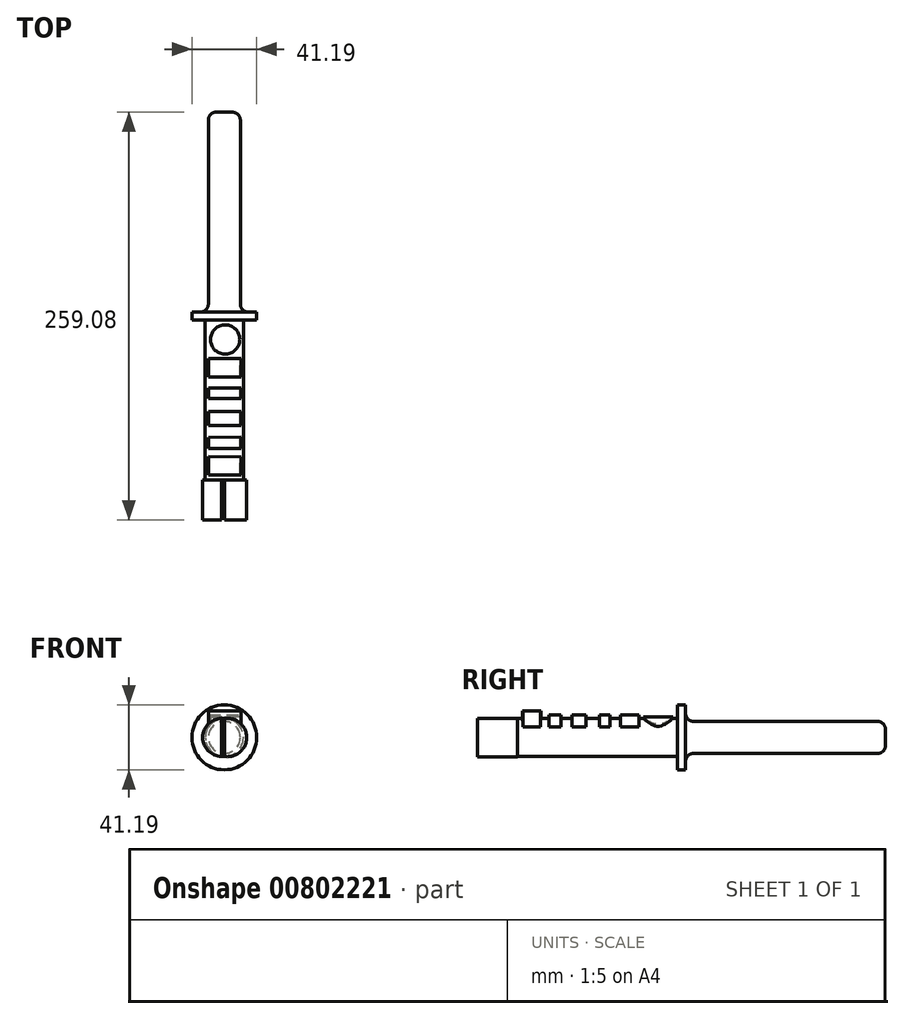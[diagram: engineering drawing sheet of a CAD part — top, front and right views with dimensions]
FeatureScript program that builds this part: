
annotation { "Feature Type Name" : "Feature", "Feature Type Description" : "" }
export const myFeature = defineFeature(function(context is Context, id is Id, definition is map)
    precondition{}
    {
        {
            var Q0;
            Q0=qCreatedBy(makeId("Front.planeOp"),FACE);
            var sketch = newSketch(context, id + "F0", { "sketchPlane" : qUnion([Q0])});
            skCircle(sketch, "E0", {"center": v(-7.9, -6.74) * mm, "radius": 12.12 * mm});
            skSolve(sketch);
        }
        {
            var Q0;
            Q0 = qSketchRegion(id + "F0", true);
            extrude(context, id + "F1", {"entities" : qUnion([Q0]), "depth" : 101.6 * mm, "offsetDistance" : 25.4 * mm});
        }
        {
            var Q0;
            Q0=makeQuery(id+"F1.opExtrude","CAP_FACE",FACE,{"disambiguationData":[OSD([sQuery(id+"F0.wireOp",EDGE,"E0")])],"isStart":true});
            var sketch = newSketch(context, id + "F2", { "sketchPlane" : qUnion([Q0])});
            skCircle(sketch, "E1", {"center": v(7.9, -6.74) * mm, "radius": 20.6 * mm});
            skSolve(sketch);
        }
        {
            var Q0;
            Q0 = qSketchRegion(id + "F2", true);
            extrude(context, id + "F3", {"entities" : qUnion([Q0]), "operationType" : NewBodyOperationType.ADD, "depth" : 5.08 * mm, "offsetDistance" : 25.4 * mm});
        }
        {
            var Q0;
            Q0=makeQuery(id+"F3.opExtrude","CAP_FACE",FACE,{"disambiguationData":[OSD([sQuery(id+"F2.wireOp",EDGE,"E1")])],"isStart":false});
            var sketch = newSketch(context, id + "F4", { "sketchPlane" : qUnion([Q0])});
            skCircle(sketch, "E2", {"center": v(7.9, -6.74) * mm, "radius": 10.16 * mm});
            skSolve(sketch);
        }
        {
            var Q0;
            Q0 = qSketchRegion(id + "F4", true);
            extrude(context, id + "F5", {"entities" : qUnion([Q0]), "operationType" : NewBodyOperationType.ADD, "depth" : 127 * mm, "offsetDistance" : 25.4 * mm});
        }
        {
            var Q0;
            Q0=makeQuery(id+"F5.opExtrude","CAP_EDGE",EDGE,{"disambiguationData":[OSD([sQuery(id+"F4.wireOp",EDGE,"E2")])],"isStart":false});
            var Q1;
            Q1=makeQuery(id+"F5.opExtrude","SWEPT_FACE",FACE,{"disambiguationData":[OSD([sQuery(id+"F4.wireOp",EDGE,"E2")])]});
            fillet(context, id + "F6", {"entities" : qUnion([Q0, Q1]), "radius" : 5.08 * mm, "tangentPropagation" : true, "allowEdgeOverflow" : false});
        }
        {
            var Q0;
            Q0=makeQuery(id+"F1.opExtrude","CAP_FACE",FACE,{"disambiguationData":[OSD([sQuery(id+"F0.wireOp",EDGE,"E0")])],"isStart":false});
            var sketch = newSketch(context, id + "F7", { "sketchPlane" : qUnion([Q0])});
            skLineSegment(sketch, "E3", {"start": v(-7.7, -18.85) * mm, "end": v(-7.7, 5.26) * mm});
            skArc(sketch, "E4", {"start": v(-7.7, -18.85) * mm, "mid": v(6.3, -6.8) * mm, "end": v(-7.7, 5.26) * mm});
            skSolve(sketch);
        }
        {
            var Q0;
            Q0 = qSketchRegion(id + "F7", true);
            extrude(context, id + "F8", {"entities" : qUnion([Q0]), "operationType" : NewBodyOperationType.ADD, "depth" : 25.4 * mm, "offsetDistance" : 25.4 * mm});
        }
        {
            var Q0;
            Q0=makeQuery(id+"F1.opExtrude","CAP_FACE",FACE,{"disambiguationData":[OSD([sQuery(id+"F0.wireOp",EDGE,"E0")])],"isStart":false});
            var sketch = newSketch(context, id + "F9", { "sketchPlane" : qUnion([Q0])});
            skLineSegment(sketch, "E5", {"start": v(-9.73, 5.24) * mm, "end": v(-9.73, -18.71) * mm});
            skArc(sketch, "E6", {"start": v(-9.73, 5.24) * mm, "mid": v(-21.63, -6.74) * mm, "end": v(-9.73, -18.71) * mm});
            skSolve(sketch);
        }
        {
            var Q0;
            Q0 = qSketchRegion(id + "F9", true);
            extrude(context, id + "F10", {"entities" : qUnion([Q0]), "operationType" : NewBodyOperationType.ADD, "depth" : 25.4 * mm, "offsetDistance" : 25.4 * mm});
        }
        {
            var Q0;
            Q0=qCreatedBy(makeId("Top.planeOp"),FACE);
            var sketch = newSketch(context, id + "F11", { "sketchPlane" : qUnion([Q0])});
            skCircle(sketch, "E7", {"center": v(-7.36, -12.35) * mm, "radius": 9.3 * mm});
            skSolve(sketch);
        }
        {
            var Q0;
            Q0 = qSketchRegion(id + "F11", true);
            extrude(context, id + "F12", {"entities" : qUnion([Q0]), "operationType" : NewBodyOperationType.ADD, "depth" : 6.35 * mm, "offsetDistance" : 25.4 * mm});
        }
        {
            var Q0;
            Q0=qCreatedBy(makeId("Top.planeOp"),FACE);
            var sketch = newSketch(context, id + "F13", { "sketchPlane" : qUnion([Q0])});
            skLineSegment(sketch, "E8", {"start": v(-17.9, -43.1) * mm, "end": v(2.87, -43.1) * mm});
            skLineSegment(sketch, "E9", {"start": v(2.87, -43.1) * mm, "end": v(2.87, -49.76) * mm});
            skLineSegment(sketch, "E10", {"start": v(2.87, -49.76) * mm, "end": v(-17.9, -49.76) * mm});
            skLineSegment(sketch, "E11", {"start": v(-17.9, -49.76) * mm, "end": v(-17.9, -43.1) * mm});
            skLineSegment(sketch, "E12", {"start": v(-17.9, -24.55) * mm, "end": v(0, -24.55) * mm});
            skLineSegment(sketch, "E13", {"start": v(0, -24.55) * mm, "end": v(2.87, -24.55) * mm});
            skLineSegment(sketch, "E14", {"start": v(2.87, -24.55) * mm, "end": v(2.87, -36.23) * mm});
            skLineSegment(sketch, "E15", {"start": v(2.87, -36.23) * mm, "end": v(-17.9, -36.23) * mm});
            skLineSegment(sketch, "E16", {"start": v(-17.9, -36.23) * mm, "end": v(-17.9, -24.55) * mm});
            skLineSegment(sketch, "E17", {"start": v(-17.9, -58.09) * mm, "end": v(-17.9, -66.95) * mm});
            skLineSegment(sketch, "E18", {"start": v(-17.9, -66.95) * mm, "end": v(2.87, -66.95) * mm});
            skLineSegment(sketch, "E19", {"start": v(2.87, -66.95) * mm, "end": v(2.87, -58.09) * mm});
            skLineSegment(sketch, "E20", {"start": v(2.87, -58.09) * mm, "end": v(-17.9, -58.09) * mm});
            skLineSegment(sketch, "E21", {"start": v(-17.9, -74.43) * mm, "end": v(-17.9, -81.58) * mm});
            skLineSegment(sketch, "E22", {"start": v(-17.9, -81.58) * mm, "end": v(2.87, -81.58) * mm});
            skLineSegment(sketch, "E23", {"start": v(2.87, -81.58) * mm, "end": v(2.87, -74.22) * mm});
            skLineSegment(sketch, "E24", {"start": v(2.87, -74.22) * mm, "end": v(-17.9, -74.43) * mm});
            skLineSegment(sketch, "E25", {"start": v(-17.9, -86.75) * mm, "end": v(-17.78, -98.52) * mm});
            skLineSegment(sketch, "E26", {"start": v(-17.78, -98.52) * mm, "end": v(2.87, -98.31) * mm});
            skLineSegment(sketch, "E27", {"start": v(2.87, -98.31) * mm, "end": v(2.75, -87.06) * mm});
            skLineSegment(sketch, "E28", {"start": v(2.75, -87.06) * mm, "end": v(-17.9, -86.75) * mm});
            skSolve(sketch);
        }
        {
            var Q0;
            Q0 = qSketchRegion(id + "F13", true);
            extrude(context, id + "F14", {"entities" : qUnion([Q0]), "operationType" : NewBodyOperationType.ADD, "depth" : 7.62 * mm, "offsetDistance" : 25.4 * mm});
        }
        {
            var Q0;
            Q0=makeQuery(id+"F14.opExtrude","CAP_FACE",FACE,{"disambiguationData":[OSD([sQuery(id+"F13.wireOp",EDGE,"E25"),sQuery(id+"F13.wireOp",EDGE,"E26"),sQuery(id+"F13.wireOp",EDGE,"E27"),sQuery(id+"F13.wireOp",EDGE,"E28")])],"isStart":false});
            var sketch = newSketch(context, id + "F15", { "sketchPlane" : qUnion([Q0])});
            skLineSegment(sketch, "E29", {"start": v(-17.9, -86.75) * mm, "end": v(2.75, -87.06) * mm});
            skLineSegment(sketch, "E30", {"start": v(2.75, -87.06) * mm, "end": v(2.87, -98.31) * mm});
            skLineSegment(sketch, "E31", {"start": v(2.87, -98.31) * mm, "end": v(-14.58, -98.49) * mm});
            skLineSegment(sketch, "E32", {"start": v(-14.58, -98.49) * mm, "end": v(-17.78, -98.52) * mm});
            skLineSegment(sketch, "E33", {"start": v(-17.78, -98.52) * mm, "end": v(-17.9, -86.75) * mm});
            skSolve(sketch);
        }
        {
            var Q0;
            Q0 = qSketchRegion(id + "F15", true);
            extrude(context, id + "F16", {"entities" : qUnion([Q0]), "operationType" : NewBodyOperationType.ADD, "depth" : 2.54 * mm, "offsetDistance" : 25.4 * mm});
        }
    });
